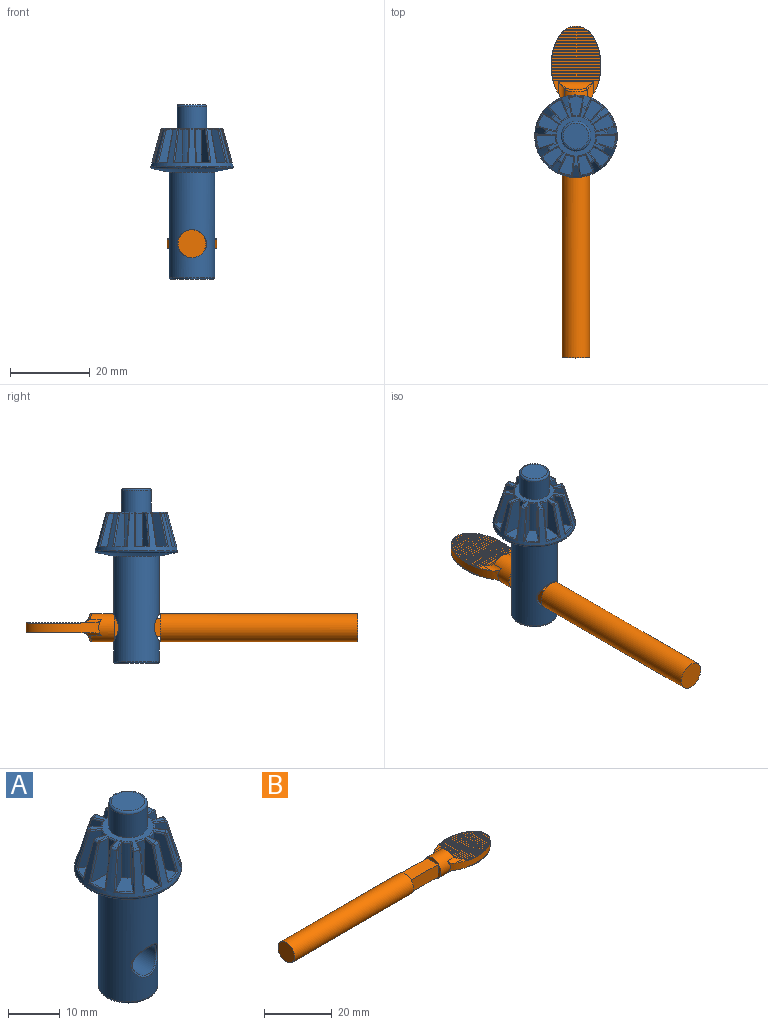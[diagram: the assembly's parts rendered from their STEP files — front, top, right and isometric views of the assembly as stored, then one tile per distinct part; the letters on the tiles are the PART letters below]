
ASSEMBLY  parts=2 mates=2
PART A: 156 faces, bbox 22.5x22.5x44 mm
  f0: cone r=7.75mm half-angle=15.4deg, axis (0,0,-1), area 196.6mm2, adj f1,f2,f3,f4,f5,f6,f7,f8
  f1: torus R=7.37mm, axis (0,0,-1), area 0.8mm2, adj f0,f13,f135,f152
  f2: torus R=7.37mm, axis (0,0,-1), area 0.8mm2, adj f0,f13,f123,f140
  f3: torus R=7.37mm, axis (0,0,-1), area 0.8mm2, adj f0,f13,f111,f128
  f4: torus R=7.37mm, axis (0,0,-1), area 0.8mm2, adj f0,f13,f99,f116
  f5: torus R=7.37mm, axis (0,0,-1), area 0.8mm2, adj f0,f13,f87,f104
  f6: torus R=7.37mm, axis (0,0,-1), area 0.8mm2, adj f0,f13,f75,f92
  f7: torus R=7.37mm, axis (0,0,-1), area 0.8mm2, adj f0,f13,f63,f80
  f8: torus R=7.37mm, axis (0,0,-1), area 0.8mm2, adj f0,f13,f51,f68
  f9: torus R=7.37mm, axis (0,0,-1), area 0.8mm2, adj f0,f13,f39,f56
  f10: torus R=7.37mm, axis (0,0,-1), area 0.8mm2, adj f0,f13,f27,f44
  f11: cylinder r=5.75mm len=26.5mm, axis (0,0,-1), area 872.2mm2, adj f12,f25,f154,f155
  f12: torus R=0.87mm, axis (0,0,-1), area 215.9mm2, adj f11,f22
  f13: plane 14.71x14.58mm, normal (0,0,1), area 57.1mm2, adj f1,f2,f3,f4,f5,f6,f7,f8
  f14: cylinder r=3.75mm len=7.5mm, axis (0,0,-1), area 129.6mm2, adj f13,f24
  f15: plane 6.5x6.5mm, normal (0,0,1), area 33.2mm2, adj f24
  f16: plane 10.5x10.5mm, normal (0,0,-1), area 86.6mm2, adj f25
  f17: cylinder r=3.25mm len=11mm, axis (0,-1,0), area 199.8mm2, adj f154,f155
  f18: plane 4.73x3.46mm, normal (0,0,1), area 12.3mm2, adj f19,f20,f21,f29,f31,f33
  f19: plane 8.25x4.51mm, normal (0.98,0.17,0), area 28.4mm2, adj f18,f21,f30,f32,f33
  f20: plane 8.25x4.51mm, normal (-0.98,0.17,0), area 28.4mm2, adj f18,f21,f26,f27,f29
  f21: cylinder r=5.25mm len=8.25mm, axis (0,0,1), area 15.1mm2, adj f18,f19,f20,f28
  f22: torus R=9.89mm, axis (0,0,1), area 50.9mm2, adj f0,f12
  f23: torus R=7.37mm, axis (0,0,-1), area 0.8mm2, adj f0,f13,f32,f147
  f24: torus R=3.25mm, axis (0,0,-1), area 17.6mm2, adj f14,f15
  f25: torus R=5.25mm, axis (0,0,1), area 27.5mm2, adj f11,f16
  f26: cylinder r=0.25mm len=2.38mm, axis (0.17,0.98,0), area 0.9mm2, adj f13,f20,f27,f28
  f27: bspline ~0.57x0.49mm, area 0.2mm2, adj f10,f20,f26,f29
  f28: torus R=5mm, axis (0,0,-1), area 0.8mm2, adj f13,f21,f26,f30
  f29: bspline ~14.91x4.26mm, area 3.4mm2, adj f0,f18,f20,f27,f31
  f30: cylinder r=0.25mm len=2.38mm, axis (0.17,-0.98,0), area 0.9mm2, adj f13,f19,f28,f32
  f31: torus R=9.9mm, axis (0,0,1), area 1.2mm2, adj f0,f18,f29,f33
  f32: bspline ~0.57x0.49mm, area 0.2mm2, adj f19,f23,f30,f33
  f33: bspline ~14.91x4.26mm, area 3.4mm2, adj f0,f18,f19,f31,f32
  f34: plane 5.28x4.7mm, normal (0,0,1), area 12.3mm2, adj f35,f36,f37,f41,f43,f45
  f35: plane 8.25x4.22mm, normal (0.92,-0.39,0), area 28.4mm2, adj f34,f37,f42,f44,f45
  f36: plane 8.25x3.36mm, normal (-0.73,0.68,0), area 28.4mm2, adj f34,f37,f38,f39,f41
  f37: cylinder r=5.25mm len=8.25mm, axis (0,0,1), area 15.1mm2, adj f34,f35,f36,f40
  f38: cylinder r=0.25mm len=1.91mm, axis (0.68,0.73,0), area 0.9mm2, adj f13,f36,f39,f40
  f39: bspline ~0.56x0.55mm, area 0.2mm2, adj f9,f36,f38,f41
  f40: torus R=5mm, axis (0,0,-1), area 0.8mm2, adj f13,f37,f38,f42
  f41: bspline ~14.91x3.18mm, area 3.4mm2, adj f0,f34,f36,f39,f43
  f42: cylinder r=0.25mm len=2.28mm, axis (-0.39,-0.92,0), area 0.9mm2, adj f13,f35,f40,f44
  f43: torus R=9.9mm, axis (0,0,1), area 1.2mm2, adj f0,f34,f41,f45
  f44: bspline ~0.65x0.46mm, area 0.2mm2, adj f10,f35,f42,f45
  f45: bspline ~14.91x4.09mm, area 3.4mm2, adj f0,f34,f35,f43,f44
  f46: plane 5.26x4.3mm, normal (0,0,1), area 12.3mm2, adj f47,f48,f49,f53,f55,f57
  f47: plane 8.25x3.77mm, normal (0.57,-0.82,0), area 28.4mm2, adj f46,f49,f54,f56,f57
  f48: plane 8.25x4.43mm, normal (-0.25,0.97,0), area 28.4mm2, adj f46,f49,f50,f51,f53
  f49: cylinder r=5.25mm len=8.25mm, axis (0,0,1), area 15.1mm2, adj f46,f47,f48,f52
  f50: cylinder r=0.25mm len=2.36mm, axis (0.97,0.25,0), area 0.9mm2, adj f13,f48,f51,f52
  f51: bspline ~0.58x0.49mm, area 0.2mm2, adj f8,f48,f50,f53
  f52: torus R=5mm, axis (0,0,-1), area 0.8mm2, adj f13,f49,f50,f54
  f53: bspline ~14.91x4.25mm, area 3.4mm2, adj f0,f46,f48,f51,f55
  f54: cylinder r=0.25mm len=2.09mm, axis (-0.82,-0.57,0), area 0.9mm2, adj f13,f47,f52,f56
  f55: torus R=9.9mm, axis (0,0,1), area 1.2mm2, adj f0,f46,f53,f57
  f56: bspline ~0.64x0.55mm, area 0.2mm2, adj f9,f47,f54,f57
  f57: bspline ~14.91x3.57mm, area 3.4mm2, adj f0,f46,f47,f55,f56
  f58: plane 4.91x3.42mm, normal (0,0,1), area 12.3mm2, adj f59,f60,f61,f65,f67,f69
  f59: plane 8.25x4.57mm, normal (0.03,-1,0), area 28.4mm2, adj f58,f61,f66,f68,f69
  f60: plane 8.25x4.35mm, normal (0.31,0.95,0), area 28.4mm2, adj f58,f61,f62,f63,f65
  f61: cylinder r=5.25mm len=8.25mm, axis (0,0,1), area 15.1mm2, adj f58,f59,f60,f64
  f62: cylinder r=0.25mm len=2.33mm, axis (0.95,-0.31,0), area 0.9mm2, adj f13,f60,f63,f64
  f63: bspline ~0.59x0.49mm, area 0.2mm2, adj f7,f60,f62,f65
  f64: torus R=5mm, axis (0,0,-1), area 0.8mm2, adj f13,f61,f62,f66
  f65: bspline ~14.91x4.11mm, area 3.4mm2, adj f0,f58,f60,f63,f67
  f66: cylinder r=0.25mm len=2.38mm, axis (-1,-0.03,0), area 0.9mm2, adj f13,f59,f64,f68
  f67: torus R=9.9mm, axis (0,0,1), area 1.2mm2, adj f0,f58,f65,f69
  f68: bspline ~0.62x0.45mm, area 0.2mm2, adj f8,f59,f66,f69
  f69: bspline ~14.91x4.33mm, area 3.4mm2, adj f0,f58,f59,f67,f68
  f70: plane 5.19x4.99mm, normal (0,0,1), area 12.3mm2, adj f71,f72,f73,f77,f79,f81
  f71: plane 8.25x3.93mm, normal (-0.51,-0.86,0), area 28.4mm2, adj f70,f73,f78,f80,f81
  f72: plane 8.25x3.55mm, normal (0.78,0.63,0), area 28.4mm2, adj f70,f73,f74,f75,f77
  f73: cylinder r=5.25mm len=8.25mm, axis (0,0,1), area 15.1mm2, adj f70,f71,f72,f76
  f74: cylinder r=0.25mm len=2mm, axis (0.63,-0.78,0), area 0.9mm2, adj f13,f72,f75,f76
  f75: bspline ~0.57x0.53mm, area 0.2mm2, adj f6,f72,f74,f77
  f76: torus R=5mm, axis (0,0,-1), area 0.8mm2, adj f13,f73,f74,f78
  f77: bspline ~14.91x3.52mm, area 3.4mm2, adj f0,f70,f72,f75,f79
  f78: cylinder r=0.25mm len=2.16mm, axis (-0.86,0.51,0), area 0.9mm2, adj f13,f71,f76,f80
  f79: torus R=9.9mm, axis (0,0,1), area 1.2mm2, adj f0,f70,f77,f81
  f80: bspline ~0.65x0.53mm, area 0.2mm2, adj f7,f71,f78,f81
  f81: bspline ~14.91x3.84mm, area 3.4mm2, adj f0,f70,f71,f79,f80
  f82: plane 5.13x3.82mm, normal (0,0,1), area 12.3mm2, adj f83,f84,f85,f89,f91,f93
  f83: plane 8.25x4.1mm, normal (-0.9,-0.44,0), area 28.4mm2, adj f82,f85,f90,f92,f93
  f84: plane 8.25x4.55mm, normal (0.99,0.11,0), area 28.4mm2, adj f82,f85,f86,f87,f89
  f85: cylinder r=5.25mm len=8.25mm, axis (0,0,1), area 15.1mm2, adj f82,f83,f84,f88
  f86: cylinder r=0.25mm len=2.38mm, axis (0.11,-0.99,0), area 0.9mm2, adj f13,f84,f87,f88
  f87: bspline ~0.55x0.49mm, area 0.2mm2, adj f5,f84,f86,f89
  f88: torus R=5mm, axis (0,0,-1), area 0.8mm2, adj f13,f85,f86,f90
  f89: bspline ~14.91x4.33mm, area 3.4mm2, adj f0,f82,f84,f87,f91
  f90: cylinder r=0.25mm len=2.24mm, axis (-0.44,0.9,0), area 0.9mm2, adj f13,f83,f88,f92
  f91: torus R=9.9mm, axis (0,0,1), area 1.2mm2, adj f0,f82,f89,f93
  f92: bspline ~0.66x0.5mm, area 0.2mm2, adj f6,f83,f90,f93
  f93: bspline ~14.91x3.88mm, area 3.4mm2, adj f0,f82,f83,f91,f92
  f94: plane 5.13x3.82mm, normal (0,0,1), area 12.3mm2, adj f95,f96,f97,f101,f103,f105
  f95: plane 8.25x4.55mm, normal (-0.99,0.11,0), area 28.4mm2, adj f94,f97,f102,f104,f105
  f96: plane 8.25x4.1mm, normal (0.9,-0.44,0), area 28.4mm2, adj f94,f97,f98,f99,f101
  f97: cylinder r=5.25mm len=8.25mm, axis (0,0,1), area 15.1mm2, adj f94,f95,f96,f100
  f98: cylinder r=0.25mm len=2.24mm, axis (-0.44,-0.9,0), area 0.9mm2, adj f13,f96,f99,f100
  f99: bspline ~0.59x0.49mm, area 0.2mm2, adj f4,f96,f98,f101
  f100: torus R=5mm, axis (0,0,-1), area 0.8mm2, adj f13,f97,f98,f102
  f101: bspline ~14.91x3.88mm, area 3.4mm2, adj f0,f94,f96,f99,f103
  f102: cylinder r=0.25mm len=2.38mm, axis (0.11,0.99,0), area 0.9mm2, adj f13,f95,f100,f104
  f103: torus R=9.9mm, axis (0,0,1), area 1.2mm2, adj f0,f94,f101,f105
  f104: bspline ~0.63x0.45mm, area 0.2mm2, adj f5,f95,f102,f105
  f105: bspline ~14.91x4.33mm, area 3.4mm2, adj f0,f94,f95,f103,f104
  f106: plane 5.19x4.99mm, normal (0,0,1), area 12.3mm2, adj f107,f108,f109,f113,f115,f117
  f107: plane 8.25x3.55mm, normal (-0.78,0.63,0), area 28.4mm2, adj f106,f109,f114,f116,f117
  f108: plane 8.25x3.93mm, normal (0.51,-0.86,0), area 28.4mm2, adj f106,f109,f110,f111,f113
  f109: cylinder r=5.25mm len=8.25mm, axis (0,0,1), area 15.1mm2, adj f106,f107,f108,f112
  f110: cylinder r=0.25mm len=2.16mm, axis (-0.86,-0.51,0), area 0.9mm2, adj f13,f108,f111,f112
  f111: bspline ~0.59x0.49mm, area 0.2mm2, adj f3,f108,f110,f113
  f112: torus R=5mm, axis (0,0,-1), area 0.8mm2, adj f13,f109,f110,f114
  f113: bspline ~14.91x3.84mm, area 3.4mm2, adj f0,f106,f108,f111,f115
  f114: cylinder r=0.25mm len=2mm, axis (0.63,0.78,0), area 0.9mm2, adj f13,f107,f112,f116
  f115: torus R=9.9mm, axis (0,0,1), area 1.2mm2, adj f0,f106,f113,f117
  f116: bspline ~0.63x0.58mm, area 0.2mm2, adj f4,f107,f114,f117
  f117: bspline ~14.91x3.52mm, area 3.4mm2, adj f0,f106,f107,f115,f116
  f118: plane 4.91x3.42mm, normal (0,0,1), area 12.3mm2, adj f119,f120,f121,f125,f127,f129
  f119: plane 8.25x4.35mm, normal (-0.31,0.95,0), area 28.4mm2, adj f118,f121,f126,f128,f129
  f120: plane 8.25x4.57mm, normal (-0.03,-1,0), area 28.4mm2, adj f118,f121,f122,f123,f125
  f121: cylinder r=5.25mm len=8.25mm, axis (0,0,1), area 15.1mm2, adj f118,f119,f120,f124
  f122: cylinder r=0.25mm len=2.38mm, axis (-1,0.03,0), area 0.9mm2, adj f13,f120,f123,f124
  f123: bspline ~0.55x0.49mm, area 0.2mm2, adj f2,f120,f122,f125
  f124: torus R=5mm, axis (0,0,-1), area 0.8mm2, adj f13,f121,f122,f126
  f125: bspline ~14.91x4.33mm, area 3.4mm2, adj f0,f118,f120,f123,f127
  f126: cylinder r=0.25mm len=2.33mm, axis (0.95,0.31,0), area 0.9mm2, adj f13,f119,f124,f128
  f127: torus R=9.9mm, axis (0,0,1), area 1.2mm2, adj f0,f118,f125,f129
  f128: bspline ~0.66x0.45mm, area 0.2mm2, adj f3,f119,f126,f129
  f129: bspline ~14.91x4.11mm, area 3.4mm2, adj f0,f118,f119,f127,f128
  f130: plane 5.26x4.3mm, normal (0,0,1), area 12.3mm2, adj f131,f132,f133,f137,f139,f141
  f131: plane 8.25x4.43mm, normal (0.25,0.97,0), area 28.4mm2, adj f130,f133,f138,f140,f141
  f132: plane 8.25x3.77mm, normal (-0.57,-0.82,0), area 28.4mm2, adj f130,f133,f134,f135,f137
  f133: cylinder r=5.25mm len=8.25mm, axis (0,0,1), area 15.1mm2, adj f130,f131,f132,f136
  f134: cylinder r=0.25mm len=2.09mm, axis (-0.82,0.57,0), area 0.9mm2, adj f13,f132,f135,f136
  f135: bspline ~0.58x0.51mm, area 0.2mm2, adj f1,f132,f134,f137
  f136: torus R=5mm, axis (0,0,-1), area 0.8mm2, adj f13,f133,f134,f138
  f137: bspline ~14.91x3.57mm, area 3.4mm2, adj f0,f130,f132,f135,f139
  f138: cylinder r=0.25mm len=2.36mm, axis (0.97,-0.25,0), area 0.9mm2, adj f13,f131,f136,f140
  f139: torus R=9.9mm, axis (0,0,1), area 1.2mm2, adj f0,f130,f137,f141
  f140: bspline ~0.65x0.45mm, area 0.2mm2, adj f2,f131,f138,f141
  f141: bspline ~14.91x4.25mm, area 3.4mm2, adj f0,f130,f131,f139,f140
  f142: plane 5.28x4.7mm, normal (0,0,1), area 12.3mm2, adj f143,f144,f145,f149,f151,f153
  f143: plane 8.25x3.36mm, normal (0.73,0.68,0), area 28.4mm2, adj f142,f145,f150,f152,f153
  f144: plane 8.25x4.22mm, normal (-0.92,-0.39,0), area 28.4mm2, adj f142,f145,f146,f147,f149
  f145: cylinder r=5.25mm len=8.25mm, axis (0,0,1), area 15.1mm2, adj f142,f143,f144,f148
  f146: cylinder r=0.25mm len=2.28mm, axis (-0.39,0.92,0), area 0.9mm2, adj f13,f144,f147,f148
  f147: bspline ~0.59x0.49mm, area 0.2mm2, adj f23,f144,f146,f149
  f148: torus R=5mm, axis (0,0,-1), area 0.8mm2, adj f13,f145,f146,f150
  f149: bspline ~14.91x4.09mm, area 3.4mm2, adj f0,f142,f144,f147,f151
  f150: cylinder r=0.25mm len=1.91mm, axis (0.68,-0.73,0), area 0.9mm2, adj f13,f143,f148,f152
  f151: torus R=9.9mm, axis (0,0,1), area 1.2mm2, adj f0,f142,f149,f153
  f152: bspline ~0.62x0.6mm, area 0.2mm2, adj f1,f143,f150,f153
  f153: bspline ~14.91x3.18mm, area 3.4mm2, adj f0,f142,f143,f151,f152
  f154: bspline ~7.33x7mm, area 10.4mm2, adj f11,f17
  f155: bspline ~7.33x7mm, area 10.4mm2, adj f11,f17
PART B: 240 faces, bbox 83.5x12.5x7 mm
  f0: cylinder r=3.5mm len=49.75mm, axis (-1,0,0), area 1094.1mm2, adj f42,f238
  f1: plane 11.5x4.58mm, normal (0,0,-1), area 52.7mm2, adj f3,f237,f238,f239
  f2: plane 11.5x4.58mm, normal (0,0,1), area 52.7mm2, adj f3,f237,f238,f239
  f3: plane 11.5x4.51mm, normal (0,1,0), area 51.8mm2, adj f1,f2,f237,f238
  f4: extruded ~18.92x12.47mm, area 105.2mm2, adj f5,f6,f7,f8,f9,f10,f11,f12
  f5: plane 11.9x0.15mm, normal (0,0,1), area 1.8mm2, adj f4,f223,f234
  f6: plane 11.91x0.15mm, normal (0,0,-1), area 1.8mm2, adj f4,f225,f236
  f7: plane 12.16x0.15mm, normal (0,0,1), area 1.8mm2, adj f4,f213,f224
  f8: plane 12.17x0.15mm, normal (0,0,-1), area 1.8mm2, adj f4,f215,f226
  f9: plane 12.35x0.15mm, normal (0,0,1), area 1.9mm2, adj f4,f203,f214
  f10: plane 12.35x0.15mm, normal (0,0,-1), area 1.9mm2, adj f4,f205,f216
  f11: plane 12.46x0.15mm, normal (0,0,1), area 1.9mm2, adj f4,f193,f204
  f12: plane 12.46x0.15mm, normal (0,0,-1), area 1.9mm2, adj f4,f195,f206
  f13: plane 12.5x0.15mm, normal (0,0,1), area 1.9mm2, adj f4,f183,f194
  f14: plane 12.5x0.15mm, normal (0,0,-1), area 1.9mm2, adj f4,f185,f196
  f15: plane 12.48x0.15mm, normal (0,0,1), area 1.9mm2, adj f4,f173,f184
  f16: plane 12.48x0.15mm, normal (0,0,-1), area 1.9mm2, adj f4,f175,f186
  f17: plane 12.39x0.15mm, normal (0,0,1), area 1.9mm2, adj f4,f163,f174
  f18: plane 12.39x0.15mm, normal (0,0,-1), area 1.9mm2, adj f4,f165,f176
  f19: plane 12.24x0.15mm, normal (0,0,1), area 1.8mm2, adj f4,f153,f164
  f20: plane 12.24x0.15mm, normal (0,0,-1), area 1.8mm2, adj f4,f155,f166
  f21: plane 12x0.15mm, normal (0,0,1), area 1.8mm2, adj f4,f143,f154
  f22: plane 12x0.15mm, normal (0,0,-1), area 1.8mm2, adj f4,f145,f156
  f23: plane 11.69x0.15mm, normal (0,0,1), area 1.7mm2, adj f4,f133,f144
  f24: plane 11.69x0.15mm, normal (0,0,-1), area 1.7mm2, adj f4,f135,f146
  f25: plane 11.29x0.15mm, normal (0,0,1), area 1.7mm2, adj f4,f123,f134
  f26: plane 11.29x0.15mm, normal (0,0,-1), area 1.7mm2, adj f4,f125,f136
  f27: plane 10.79x0.15mm, normal (0,0,1), area 1.6mm2, adj f4,f113,f124
  f28: plane 10.79x0.15mm, normal (0,0,-1), area 1.6mm2, adj f4,f115,f126
  f29: plane 10.18x0.15mm, normal (0,0,1), area 1.5mm2, adj f4,f103,f114
  f30: plane 10.18x0.15mm, normal (0,0,-1), area 1.5mm2, adj f4,f105,f116
  f31: plane 9.45x0.15mm, normal (0,0,1), area 1.4mm2, adj f4,f93,f104
  f32: plane 9.45x0.15mm, normal (0,0,-1), area 1.4mm2, adj f4,f95,f106
  f33: plane 8.54x0.15mm, normal (0,0,1), area 1.3mm2, adj f4,f83,f94
  f34: plane 8.55x0.15mm, normal (0,0,-1), area 1.3mm2, adj f4,f85,f96
  f35: plane 7.42x0.15mm, normal (0,0,1), area 1.1mm2, adj f4,f73,f84
  f36: plane 7.42x0.15mm, normal (0,0,-1), area 1.1mm2, adj f4,f75,f86
  f37: plane 5.94x0.15mm, normal (0,0,1), area 0.9mm2, adj f4,f63,f74
  f38: plane 5.94x0.15mm, normal (0,0,-1), area 0.9mm2, adj f4,f65,f76
  f39: plane 3.71x0.45mm, normal (0,0,1), area 1.1mm2, adj f4,f64
  f40: plane 3.72x0.45mm, normal (0,0,-1), area 1.1mm2, adj f4,f66
  f41: cylinder r=3.5mm len=7mm, axis (-1,0,0), area 110.9mm2, adj f4,f46,f47,f49,f50,f52,f55,f237
  f42: plane 7x7mm, normal (-1,0,0), area 38.5mm2, adj f0
  f43: plane 11.56x3.24mm, normal (0,0,1), area 6.7mm2, adj f4,f45,f46,f50,f233
  f44: plane 11.57x3.25mm, normal (0,0,-1), area 6.7mm2, adj f4,f47,f48,f49,f235
  f45: cylinder r=2mm len=8.87mm, axis (0,1,0), area 16.3mm2, adj f43,f51,f52,f53
  f46: cylinder r=2mm len=4.92mm, axis (-1,0,0), area 5.6mm2, adj f4,f41,f43,f53
  f47: cylinder r=2mm len=4.92mm, axis (-1,0,0), area 5.6mm2, adj f4,f41,f44,f54
  f48: cylinder r=2mm len=8.87mm, axis (0,-1,0), area 16.3mm2, adj f44,f54,f55,f56
  f49: cylinder r=2mm len=4.92mm, axis (-1,0,0), area 5.6mm2, adj f4,f41,f44,f56
  f50: cylinder r=2mm len=4.92mm, axis (-1,0,0), area 5.6mm2, adj f4,f41,f43,f51
  f51: bspline ~2.12x2.12mm, area 0.5mm2, adj f45,f50,f52
  f52: bspline ~6.04x1.82mm, area 4.2mm2, adj f41,f45,f51,f53
  f53: bspline ~2.12x2.12mm, area 0.5mm2, adj f45,f46,f52
  f54: bspline ~2.12x2.12mm, area 0.5mm2, adj f47,f48,f55
  f55: bspline ~6.14x1.82mm, area 4.2mm2, adj f41,f48,f54,f56
  f56: bspline ~2.12x2.12mm, area 0.5mm2, adj f48,f49,f55
  f57: plane 5.45x0.5mm, normal (0,0,1), area 2.4mm2, adj f4,f58,f59
  f58: plane 5.45x0.09mm, normal (1,0,0), area 0.5mm2, adj f4,f57,f63
  f59: plane 3.91x0.09mm, normal (-1,0,0), area 0.3mm2, adj f4,f57,f64
  f60: plane 5.45x0.5mm, normal (0,0,-1), area 2.4mm2, adj f4,f61,f62
  f61: plane 5.45x0.09mm, normal (1,0,0), area 0.5mm2, adj f4,f60,f65
  f62: plane 3.91x0.09mm, normal (-1,0,0), area 0.3mm2, adj f4,f60,f66
  f63: cylinder r=0.05mm len=5.58mm, axis (0,1,0), area 0.4mm2, adj f4,f37,f58
  f64: cylinder r=0.05mm len=3.91mm, axis (0,-1,0), area 0.3mm2, adj f4,f39,f59
  f65: cylinder r=0.05mm len=5.58mm, axis (0,1,0), area 0.4mm2, adj f4,f38,f61
  f66: cylinder r=0.05mm len=3.91mm, axis (0,-1,0), area 0.3mm2, adj f4,f40,f62
  f67: plane 7.07x0.5mm, normal (0,0,1), area 3.3mm2, adj f4,f68,f69
  f68: plane 7.07x0.09mm, normal (1,0,0), area 0.6mm2, adj f4,f67,f73
  f69: plane 6.05x0.09mm, normal (-1,0,0), area 0.5mm2, adj f4,f67,f74
  f70: plane 7.07x0.5mm, normal (0,0,-1), area 3.3mm2, adj f4,f71,f72
  f71: plane 7.07x0.09mm, normal (1,0,0), area 0.6mm2, adj f4,f70,f75
  f72: plane 6.05x0.09mm, normal (-1,0,0), area 0.5mm2, adj f4,f70,f76
  f73: cylinder r=0.05mm len=7.16mm, axis (0,1,0), area 0.6mm2, adj f4,f35,f68
  f74: cylinder r=0.05mm len=6.05mm, axis (0,-1,0), area 0.5mm2, adj f4,f37,f69
  f75: cylinder r=0.05mm len=7.16mm, axis (0,1,0), area 0.6mm2, adj f4,f36,f71
  f76: cylinder r=0.05mm len=6.05mm, axis (0,-1,0), area 0.5mm2, adj f4,f38,f72
  f77: plane 8.27x0.5mm, normal (0,0,1), area 3.9mm2, adj f4,f78,f79
  f78: plane 8.27x0.09mm, normal (1,0,0), area 0.7mm2, adj f4,f77,f83
  f79: plane 7.5x0.09mm, normal (-1,0,0), area 0.7mm2, adj f4,f77,f84
  f80: plane 8.27x0.5mm, normal (0,0,-1), area 3.9mm2, adj f4,f81,f82
  f81: plane 8.27x0.09mm, normal (1,0,0), area 0.7mm2, adj f4,f80,f85
  f82: plane 7.5x0.09mm, normal (-1,0,0), area 0.6mm2, adj f4,f80,f86
  f83: cylinder r=0.05mm len=8.34mm, axis (0,1,0), area 0.7mm2, adj f4,f33,f78
  f84: cylinder r=0.05mm len=7.5mm, axis (0,-1,0), area 0.6mm2, adj f4,f35,f79
  f85: cylinder r=0.05mm len=8.34mm, axis (0,1,0), area 0.7mm2, adj f4,f34,f81
  f86: cylinder r=0.05mm len=7.5mm, axis (0,-1,0), area 0.6mm2, adj f4,f36,f82
  f87: plane 9.22x0.5mm, normal (0,0,1), area 4.5mm2, adj f4,f88,f89
  f88: plane 9.22x0.09mm, normal (1,0,0), area 0.8mm2, adj f4,f87,f93
  f89: plane 8.61x0.09mm, normal (-1,0,0), area 0.8mm2, adj f4,f87,f94
  f90: plane 9.22x0.5mm, normal (0,0,-1), area 4.5mm2, adj f4,f91,f92
  f91: plane 9.22x0.09mm, normal (1,0,0), area 0.8mm2, adj f4,f90,f95
  f92: plane 8.61x0.09mm, normal (-1,0,0), area 0.7mm2, adj f4,f90,f96
  f93: cylinder r=0.05mm len=9.28mm, axis (0,1,0), area 0.7mm2, adj f4,f31,f88
  f94: cylinder r=0.05mm len=8.61mm, axis (0,-1,0), area 0.7mm2, adj f4,f33,f89
  f95: cylinder r=0.05mm len=9.28mm, axis (0,1,0), area 0.7mm2, adj f4,f32,f91
  f96: cylinder r=0.05mm len=8.61mm, axis (0,-1,0), area 0.7mm2, adj f4,f34,f92
  f97: plane 10x0.5mm, normal (0,0,1), area 4.9mm2, adj f4,f98,f99
  f98: plane 10x0.09mm, normal (1,0,0), area 0.9mm2, adj f4,f97,f103
  f99: plane 9.5x0.09mm, normal (-1,0,0), area 0.8mm2, adj f4,f97,f104
  f100: plane 10x0.5mm, normal (0,0,-1), area 4.9mm2, adj f4,f101,f102
  f101: plane 10x0.09mm, normal (1,0,0), area 0.9mm2, adj f4,f100,f105
  f102: plane 9.5x0.09mm, normal (-1,0,0), area 0.8mm2, adj f4,f100,f106
  f103: cylinder r=0.05mm len=10.05mm, axis (0,1,0), area 0.8mm2, adj f4,f29,f98
  f104: cylinder r=0.05mm len=9.5mm, axis (0,-1,0), area 0.7mm2, adj f4,f31,f99
  f105: cylinder r=0.05mm len=10.05mm, axis (0,1,0), area 0.8mm2, adj f4,f30,f101
  f106: cylinder r=0.05mm len=9.5mm, axis (0,-1,0), area 0.7mm2, adj f4,f32,f102
  f107: plane 10.64x0.5mm, normal (0,0,1), area 5.2mm2, adj f4,f108,f109
  f108: plane 10.64x0.09mm, normal (1,0,0), area 0.9mm2, adj f4,f107,f113
  f109: plane 10.23x0.09mm, normal (-1,0,0), area 0.9mm2, adj f4,f107,f114
  f110: plane 10.64x0.5mm, normal (0,0,-1), area 5.2mm2, adj f4,f111,f112
  f111: plane 10.64x0.09mm, normal (1,0,0), area 0.9mm2, adj f4,f110,f115
  f112: plane 10.23x0.09mm, normal (-1,0,0), area 0.9mm2, adj f4,f110,f116
  f113: cylinder r=0.05mm len=10.68mm, axis (0,1,0), area 0.8mm2, adj f4,f27,f108
  f114: cylinder r=0.05mm len=10.23mm, axis (0,-1,0), area 0.8mm2, adj f4,f29,f109
  f115: cylinder r=0.05mm len=10.68mm, axis (0,1,0), area 0.8mm2, adj f4,f28,f111
  f116: cylinder r=0.05mm len=10.23mm, axis (0,-1,0), area 0.8mm2, adj f4,f30,f112
  f117: plane 11.16x0.5mm, normal (0,0,1), area 5.5mm2, adj f4,f118,f119
  f118: plane 11.16x0.09mm, normal (1,0,0), area 1mm2, adj f4,f117,f123
  f119: plane 10.83x0.09mm, normal (-1,0,0), area 1mm2, adj f4,f117,f124
  f120: plane 11.16x0.5mm, normal (0,0,-1), area 5.5mm2, adj f4,f121,f122
  f121: plane 11.16x0.09mm, normal (1,0,0), area 1mm2, adj f4,f120,f125
  f122: plane 10.83x0.09mm, normal (-1,0,0), area 0.9mm2, adj f4,f120,f126
  f123: cylinder r=0.05mm len=11.2mm, axis (0,1,0), area 0.9mm2, adj f4,f25,f118
  f124: cylinder r=0.05mm len=10.83mm, axis (0,-1,0), area 0.8mm2, adj f4,f27,f119
  f125: cylinder r=0.05mm len=11.2mm, axis (0,1,0), area 0.9mm2, adj f4,f26,f121
  f126: cylinder r=0.05mm len=10.83mm, axis (0,-1,0), area 0.8mm2, adj f4,f28,f122
  f127: plane 11.59x0.5mm, normal (0,0,1), area 5.7mm2, adj f4,f128,f129
  f128: plane 11.59x0.09mm, normal (1,0,0), area 1mm2, adj f4,f127,f133
  f129: plane 11.32x0.09mm, normal (-1,0,0), area 1mm2, adj f4,f127,f134
  f130: plane 11.59x0.5mm, normal (0,0,-1), area 5.7mm2, adj f4,f131,f132
  f131: plane 11.59x0.09mm, normal (1,0,0), area 1mm2, adj f4,f130,f135
  f132: plane 11.32x0.09mm, normal (-1,0,0), area 1mm2, adj f4,f130,f136
  f133: cylinder r=0.05mm len=11.61mm, axis (0,1,0), area 0.9mm2, adj f4,f23,f128
  f134: cylinder r=0.05mm len=11.32mm, axis (0,-1,0), area 0.9mm2, adj f4,f25,f129
  f135: cylinder r=0.05mm len=11.61mm, axis (0,1,0), area 0.9mm2, adj f4,f24,f131
  f136: cylinder r=0.05mm len=11.32mm, axis (0,-1,0), area 0.9mm2, adj f4,f26,f132
  f137: plane 11.92x0.5mm, normal (0,0,1), area 5.9mm2, adj f4,f138,f139
  f138: plane 11.92x0.09mm, normal (1,0,0), area 1.1mm2, adj f4,f137,f143
  f139: plane 11.71x0.09mm, normal (-1,0,0), area 1mm2, adj f4,f137,f144
  f140: plane 11.92x0.5mm, normal (0,0,-1), area 5.9mm2, adj f4,f141,f142
  f141: plane 11.92x0.09mm, normal (1,0,0), area 1mm2, adj f4,f140,f145
  f142: plane 11.71x0.09mm, normal (-1,0,0), area 1mm2, adj f4,f140,f146
  f143: cylinder r=0.05mm len=11.94mm, axis (0,1,0), area 0.9mm2, adj f4,f21,f138
  f144: cylinder r=0.05mm len=11.71mm, axis (0,-1,0), area 0.9mm2, adj f4,f23,f139
  f145: cylinder r=0.05mm len=11.94mm, axis (0,1,0), area 0.9mm2, adj f4,f22,f141
  f146: cylinder r=0.05mm len=11.71mm, axis (0,-1,0), area 0.9mm2, adj f4,f24,f142
  f147: plane 12.18x0.5mm, normal (0,0,1), area 6.1mm2, adj f4,f148,f149
  f148: plane 12.18x0.09mm, normal (1,0,0), area 1.1mm2, adj f4,f147,f153
  f149: plane 12.02x0.09mm, normal (-1,0,0), area 1.1mm2, adj f4,f147,f154
  f150: plane 12.18x0.5mm, normal (0,0,-1), area 6.1mm2, adj f4,f151,f152
  f151: plane 12.18x0.09mm, normal (1,0,0), area 1mm2, adj f4,f150,f155
  f152: plane 12.02x0.09mm, normal (-1,0,0), area 1mm2, adj f4,f150,f156
  f153: cylinder r=0.05mm len=12.19mm, axis (0,1,0), area 1mm2, adj f4,f19,f148
  f154: cylinder r=0.05mm len=12.02mm, axis (0,-1,0), area 0.9mm2, adj f4,f21,f149
  f155: cylinder r=0.05mm len=12.19mm, axis (0,1,0), area 1mm2, adj f4,f20,f151
  f156: cylinder r=0.05mm len=12.02mm, axis (0,-1,0), area 0.9mm2, adj f4,f22,f152
  f157: plane 12.36x0.5mm, normal (0,0,1), area 6.2mm2, adj f4,f158,f159
  f158: plane 12.36x0.09mm, normal (1,0,0), area 1.1mm2, adj f4,f157,f163
  f159: plane 12.25x0.09mm, normal (-1,0,0), area 1.1mm2, adj f4,f157,f164
  f160: plane 12.36x0.5mm, normal (0,0,-1), area 6.2mm2, adj f4,f161,f162
  f161: plane 12.36x0.09mm, normal (1,0,0), area 1.1mm2, adj f4,f160,f165
  f162: plane 12.25x0.09mm, normal (-1,0,0), area 1.1mm2, adj f4,f160,f166
  f163: cylinder r=0.05mm len=12.37mm, axis (0,1,0), area 1mm2, adj f4,f17,f158
  f164: cylinder r=0.05mm len=12.25mm, axis (0,-1,0), area 1mm2, adj f4,f19,f159
  f165: cylinder r=0.05mm len=12.37mm, axis (0,1,0), area 1mm2, adj f4,f18,f161
  f166: cylinder r=0.05mm len=12.25mm, axis (0,-1,0), area 1mm2, adj f4,f20,f162
  f167: plane 12.47x0.5mm, normal (0,0,1), area 6.2mm2, adj f4,f168,f169
  f168: plane 12.47x0.09mm, normal (1,0,0), area 1.1mm2, adj f4,f167,f173
  f169: plane 12.4x0.09mm, normal (-1,0,0), area 1.1mm2, adj f4,f167,f174
  f170: plane 12.47x0.5mm, normal (0,0,-1), area 6.2mm2, adj f4,f171,f172
  f171: plane 12.47x0.09mm, normal (1,0,0), area 1.1mm2, adj f4,f170,f175
  f172: plane 12.4x0.09mm, normal (-1,0,0), area 1.1mm2, adj f4,f170,f176
  f173: cylinder r=0.05mm len=12.47mm, axis (0,1,0), area 1mm2, adj f4,f15,f168
  f174: cylinder r=0.05mm len=12.4mm, axis (0,-1,0), area 1mm2, adj f4,f17,f169
  f175: cylinder r=0.05mm len=12.47mm, axis (0,1,0), area 1mm2, adj f4,f16,f171
  f176: cylinder r=0.05mm len=12.4mm, axis (0,-1,0), area 1mm2, adj f4,f18,f172
  f177: plane 12.5x0.5mm, normal (0,0,1), area 6.2mm2, adj f4,f178,f179
  f178: plane 12.5x0.09mm, normal (1,0,0), area 1.1mm2, adj f4,f177,f183
  f179: plane 12.48x0.09mm, normal (-1,0,0), area 1.1mm2, adj f4,f177,f184
  f180: plane 12.5x0.5mm, normal (0,0,-1), area 6.2mm2, adj f4,f181,f182
  f181: plane 12.5x0.09mm, normal (1,0,0), area 1.1mm2, adj f4,f180,f185
  f182: plane 12.48x0.09mm, normal (-1,0,0), area 1.1mm2, adj f4,f180,f186
  f183: cylinder r=0.05mm len=12.5mm, axis (0,1,0), area 1mm2, adj f4,f13,f178
  f184: cylinder r=0.05mm len=12.48mm, axis (0,-1,0), area 1mm2, adj f4,f15,f179
  f185: cylinder r=0.05mm len=12.5mm, axis (0,1,0), area 1mm2, adj f4,f14,f181
  f186: cylinder r=0.05mm len=12.48mm, axis (0,-1,0), area 1mm2, adj f4,f16,f182
  f187: plane 12.5x0.5mm, normal (0,0,1), area 6.2mm2, adj f4,f188,f189
  f188: plane 12.46x0.09mm, normal (1,0,0), area 1.1mm2, adj f4,f187,f193
  f189: plane 12.5x0.09mm, normal (-1,0,0), area 1.1mm2, adj f4,f187,f194
  f190: plane 12.5x0.5mm, normal (0,0,-1), area 6.2mm2, adj f4,f191,f192
  f191: plane 12.46x0.09mm, normal (1,0,0), area 1.1mm2, adj f4,f190,f195
  f192: plane 12.5x0.09mm, normal (-1,0,0), area 1.1mm2, adj f4,f190,f196
  f193: cylinder r=0.05mm len=12.46mm, axis (0,1,0), area 1mm2, adj f4,f11,f188
  f194: cylinder r=0.05mm len=12.5mm, axis (0,-1,0), area 1mm2, adj f4,f13,f189
  f195: cylinder r=0.05mm len=12.46mm, axis (0,1,0), area 1mm2, adj f4,f12,f191
  f196: cylinder r=0.05mm len=12.5mm, axis (0,-1,0), area 1mm2, adj f4,f14,f192
  f197: plane 12.44x0.5mm, normal (0,0,1), area 6.2mm2, adj f4,f198,f199
  f198: plane 12.36x0.09mm, normal (1,0,0), area 1.1mm2, adj f4,f197,f203
  f199: plane 12.44x0.09mm, normal (-1,0,0), area 1.1mm2, adj f4,f197,f204
  f200: plane 12.44x0.5mm, normal (0,0,-1), area 6.2mm2, adj f4,f201,f202
  f201: plane 12.36x0.09mm, normal (1,0,0), area 1.1mm2, adj f4,f200,f205
  f202: plane 12.44x0.09mm, normal (-1,0,0), area 1.1mm2, adj f4,f200,f206
  f203: cylinder r=0.05mm len=12.36mm, axis (0,1,0), area 1mm2, adj f4,f9,f198
  f204: cylinder r=0.05mm len=12.44mm, axis (0,-1,0), area 1mm2, adj f4,f11,f199
  f205: cylinder r=0.05mm len=12.36mm, axis (0,1,0), area 1mm2, adj f4,f10,f201
  f206: cylinder r=0.05mm len=12.44mm, axis (0,-1,0), area 1mm2, adj f4,f12,f202
  f207: plane 12.31x0.5mm, normal (0,0,1), area 6.1mm2, adj f4,f208,f209
  f208: plane 12.18x0.09mm, normal (1,0,0), area 1.1mm2, adj f4,f207,f213
  f209: plane 12.31x0.09mm, normal (-1,0,0), area 1.1mm2, adj f4,f207,f214
  f210: plane 12.31x0.5mm, normal (0,0,-1), area 6.1mm2, adj f4,f211,f212
  f211: plane 12.18x0.09mm, normal (1,0,0), area 1mm2, adj f4,f210,f215
  f212: plane 12.31x0.09mm, normal (-1,0,0), area 1.1mm2, adj f4,f210,f216
  f213: cylinder r=0.05mm len=12.18mm, axis (0,1,0), area 1mm2, adj f4,f7,f208
  f214: cylinder r=0.05mm len=12.32mm, axis (0,-1,0), area 1mm2, adj f4,f9,f209
  f215: cylinder r=0.05mm len=12.18mm, axis (0,1,0), area 1mm2, adj f4,f8,f211
  f216: cylinder r=0.05mm len=12.32mm, axis (0,-1,0), area 1mm2, adj f4,f10,f212
  f217: plane 12.1x0.5mm, normal (0,0,1), area 6mm2, adj f4,f218,f219
  f218: plane 11.92x0.09mm, normal (1,0,0), area 1.1mm2, adj f4,f217,f223
  f219: plane 12.1x0.09mm, normal (-1,0,0), area 1.1mm2, adj f4,f217,f224
  f220: plane 12.1x0.5mm, normal (0,0,-1), area 6mm2, adj f4,f221,f222
  f221: plane 11.92x0.09mm, normal (1,0,0), area 1mm2, adj f4,f220,f225
  f222: plane 12.1x0.09mm, normal (-1,0,0), area 1mm2, adj f4,f220,f226
  f223: cylinder r=0.05mm len=11.92mm, axis (0,1,0), area 0.9mm2, adj f4,f5,f218
  f224: cylinder r=0.05mm len=12.12mm, axis (0,-1,0), area 1mm2, adj f4,f7,f219
  f225: cylinder r=0.05mm len=11.92mm, axis (0,1,0), area 0.9mm2, adj f4,f6,f221
  f226: cylinder r=0.05mm len=12.12mm, axis (0,-1,0), area 1mm2, adj f4,f8,f222
  f227: plane 11.82x0.5mm, normal (0,0,1), area 5.9mm2, adj f4,f228,f229
  f228: plane 11.59x0.09mm, normal (1,0,0), area 1mm2, adj f4,f227,f233
  f229: plane 11.82x0.09mm, normal (-1,0,0), area 1mm2, adj f4,f227,f234
  f230: plane 11.82x0.5mm, normal (0,0,-1), area 5.9mm2, adj f4,f231,f232
  f231: plane 11.59x0.09mm, normal (1,0,0), area 1mm2, adj f4,f230,f235
  f232: plane 11.82x0.09mm, normal (-1,0,0), area 1mm2, adj f4,f230,f236
  f233: cylinder r=0.05mm len=11.59mm, axis (0,1,0), area 0.9mm2, adj f4,f43,f228
  f234: cylinder r=0.05mm len=11.84mm, axis (0,-1,0), area 0.9mm2, adj f4,f5,f229
  f235: cylinder r=0.05mm len=11.59mm, axis (0,1,0), area 0.9mm2, adj f4,f44,f231
  f236: cylinder r=0.05mm len=11.84mm, axis (0,-1,0), area 0.9mm2, adj f4,f6,f232
  f237: plane 7x7mm, normal (-1,0,0), area 17.8mm2, adj f1,f2,f3,f41,f239
  f238: plane 7x7mm, normal (1,0,0), area 17.8mm2, adj f0,f1,f2,f3,f239
  f239: plane 11.5x4.51mm, normal (0,-1,0), area 51.8mm2, adj f1,f2,f237,f238
PLACE A t=(-22.02,-2.69,-6.96)mm fixed
PLACE B rot(axis=(0.71,0.71,0),180deg) t=(-22.02,-58.42,2.04)mm
MATE parallel A.f17 <-> B.f0  axis (0,-1,0) through (-22.02,-2.69,2.04)mm
MATE slider B.f0 <-> A.f17  axis (0,-1,0) through (-22.02,-33.55,2.04)mm
